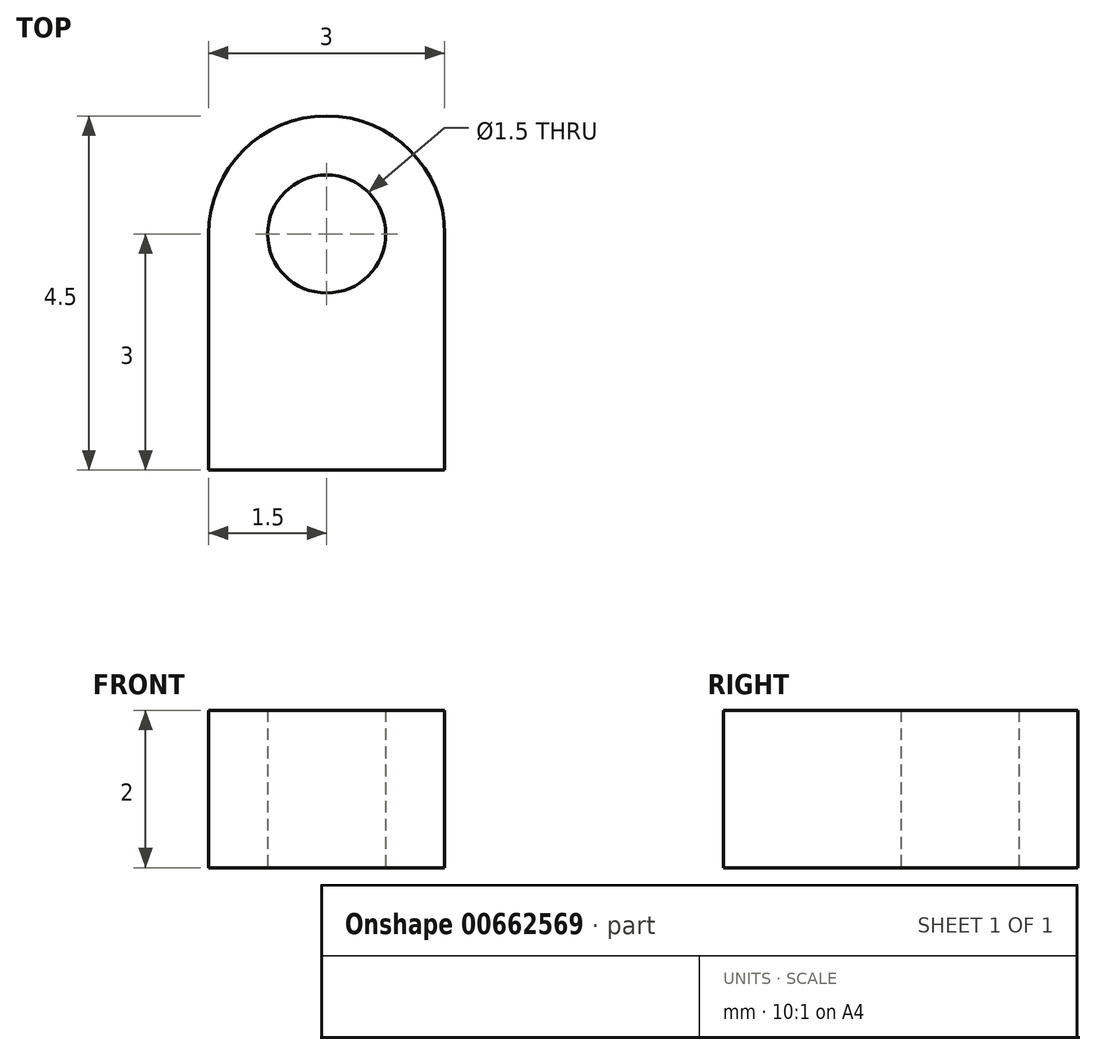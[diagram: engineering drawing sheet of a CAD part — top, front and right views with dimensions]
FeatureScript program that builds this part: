
annotation { "Feature Type Name" : "Feature", "Feature Type Description" : "" }
export const myFeature = defineFeature(function(context is Context, id is Id, definition is map)
    precondition{}
    {
        {
            var Q0;
            Q0=qCreatedBy(makeId("Top.planeOp"),FACE);
            var sketch = newSketch(context, id + "F0", { "sketchPlane" : qUnion([Q0])});
            skLineSegment(sketch, "E0", {"start": v(0, 0) * mm, "end": v(3, 0) * mm});
            skLineSegment(sketch, "E1", {"start": v(3, 0) * mm, "end": v(3, 3) * mm});
            skLineSegment(sketch, "E2", {"start": v(0, 0) * mm, "end": v(0, 3) * mm});
            skArc(sketch, "E3", {"start": v(3, 3) * mm, "mid": v(1.5, 4.5) * mm, "end": v(0, 3) * mm});
            skPoint(sketch, "E3.centerSnap0", {"position": v(1.5, 0) * mm});
            skCircle(sketch, "E4", {"center": v(1.5, 3) * mm, "radius": 0.75 * mm});
            skSolve(sketch);
        }
        {
            var Q0;
            Q0=makeQuery(id+"F0.imprint","IMPRINT",FACE,{"disambiguationData":[TD([[makeQuery(id+"F0.imprint","IMPRINT",EDGE,{"derivedFrom":sQuery(id+"F0.wireOp",EDGE,"E0")}),1.0]])]});
            extrude(context, id + "F1", {"entities" : qUnion([Q0]), "depth" : 2 * mm, "offsetDistance" : 25 * mm});
        }
    });
